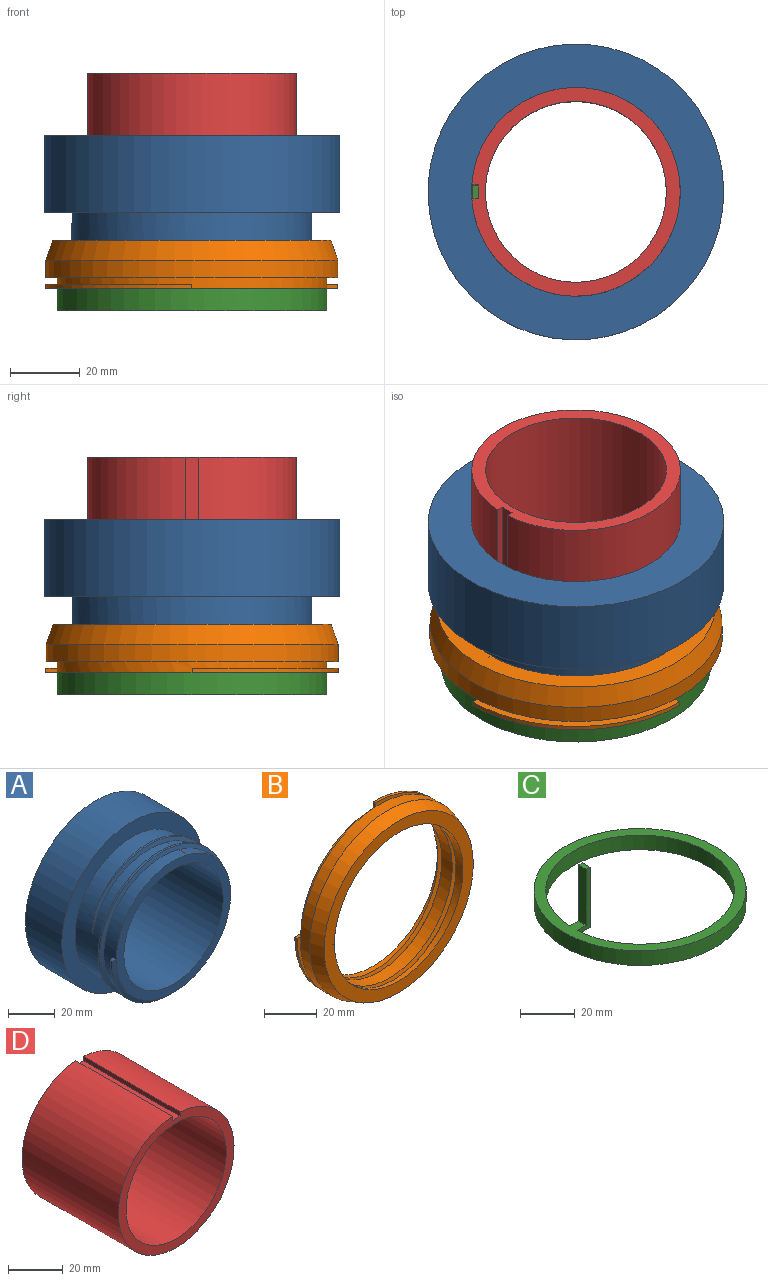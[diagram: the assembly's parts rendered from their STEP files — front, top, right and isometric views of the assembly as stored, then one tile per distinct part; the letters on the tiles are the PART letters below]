
ASSEMBLY  parts=4 mates=4
PART A: 13 faces, bbox 85.2x47.2x85.2 mm
  f0: bspline ~73x73mm, area 802.4mm2, adj f2,f4,f6,f8,f9
  f1: bspline ~73x73mm, area 892.7mm2, adj f2,f4,f5,f6,f8,f9
  f2: cylinder r=36.5mm len=73mm, axis (0,1,0), area 421.7mm2, adj f0,f1,f8,f9
  f3: cylinder r=30mm len=60mm, axis (0,1,0), area 8859.3mm2, adj f7,f11
  f4: cylinder r=34.5mm len=69mm, axis (0,1,0), area 2934.4mm2, adj f0,f1,f6,f9,f12
  f5: cylinder r=34.5mm len=69mm, axis (0,1,0), area 415.6mm2, adj f1,f6,f7
  f6: cylinder r=34.5mm len=69mm, axis (0,1,0), area 1270.9mm2, adj f0,f1,f4,f5,f7,f8
  f7: plane 69x69mm, normal (0,-1,0), area 911.8mm2, adj f3,f5,f6
  f8: plane 2x2mm, normal (0,0,1), area 3mm2, adj f0,f1,f2,f6
  f9: plane 42.8x30.41mm, normal (0,1,0), area 87.8mm2, adj f0,f1,f2,f4
  f10: cylinder r=42.5mm len=85mm, axis (0,-1,0), area 5874.8mm2, adj f11,f12
  f11: plane 85x85mm, normal (0,1,0), area 2847.1mm2, adj f3,f10
  f12: plane 85x85mm, normal (0,-1,0), area 1935.2mm2, adj f4,f10
PART B: 19 faces, bbox 84.1x14.9x84.1 mm
  f0: plane 84.13x84.13mm, normal (0,1,0), area 1296.7mm2, adj f1,f2,f7,f8,f9,f11,f12,f13
  f1: cylinder r=34.5mm len=69mm, axis (0,1,0), area 2253mm2, adj f0,f4,f15,f16,f18
  f2: cylinder r=38.75mm len=77.5mm, axis (0,1,0), area 584.3mm2, adj f0,f5,f7,f8,f10,f11,f12,f14
  f3: cylinder r=42mm len=84mm, axis (0,1,0), area 1319.5mm2, adj f5,f6
  f4: plane 80x80mm, normal (0,-1,0), area 1287.3mm2, adj f1,f6
  f5: plane 84x84mm, normal (0,1,0), area 824.5mm2, adj f2,f3
  f6: cone r=40mm half-angle=19.2deg, axis (0,1,0), area 1568.3mm2, adj f3,f4
  f7: plane 3.25x1.2mm, normal (-1,0,0), area 3.9mm2, adj f0,f2,f9,f10
  f8: plane 3.25x1.2mm, normal (0,0,-1), area 3.9mm2, adj f0,f2,f9,f10
  f9: cylinder r=42.07mm len=42mm, axis (0,1,0), area 79.1mm2, adj f0,f7,f8,f10
  f10: plane 42x42mm, normal (0,-1,0), area 204.6mm2, adj f2,f7,f8,f9
  f11: plane 3.25x1.2mm, normal (0,0,1), area 3.9mm2, adj f0,f2,f13,f14
  f12: plane 3.25x1.2mm, normal (1,0,0), area 3.9mm2, adj f0,f2,f13,f14
  f13: cylinder r=42.2mm len=42mm, axis (0,1,0), area 79.1mm2, adj f0,f11,f12,f14
  f14: plane 42x42mm, normal (0,-1,0), area 202.1mm2, adj f2,f11,f12,f13
  f15: bspline ~73x73mm, area 726.7mm2, adj f0,f1,f17,f18
  f16: bspline ~73x73mm, area 817.2mm2, adj f0,f1,f17,f18
  f17: cylinder r=36.5mm len=73mm, axis (0,1,0), area 384.8mm2, adj f0,f15,f16,f18
  f18: plane 2x2mm, normal (0,0,-1), area 3mm2, adj f1,f15,f16,f17
PART C: 10 faces, bbox 77.5x77.5x31.5 mm
  f0: plane 77.5x77.5mm, normal (0,0,1), area 996.6mm2, adj f1,f2,f5,f6,f8
  f1: cylinder r=34.5mm len=69mm, axis (0,0,-1), area 1401mm2, adj f0,f3,f4,f5,f6
  f2: cylinder r=38.75mm len=77.5mm, axis (0,0,-1), area 1582.6mm2, adj f0,f3
  f3: plane 77.5x77.5mm, normal (0,0,-1), area 978mm2, adj f1,f2
  f4: plane 6.67x4mm, normal (0,0,-1), area 26.6mm2, adj f1,f5,f6,f7
  f5: plane 27x6.61mm, normal (0,-1,0), area 63.2mm2, adj f0,f1,f4,f7,f8,f9
  f6: plane 27x6.61mm, normal (0,1,0), area 63.2mm2, adj f0,f1,f4,f7,f8,f9
  f7: plane 27x4mm, normal (1,0,0), area 108mm2, adj f4,f5,f6,f9
  f8: plane 25x4mm, normal (-1,0,0), area 100mm2, adj f0,f5,f6,f9
  f9: plane 4x2mm, normal (0,0,1), area 8mm2, adj f5,f6,f7,f8
PART D: 7 faces, bbox 60x50x59.9 mm
  f0: cylinder r=30mm len=60mm, axis (0,1,0), area 9224.6mm2, adj f1,f2,f4,f5
  f1: plane 60x59.93mm, normal (0,-1,0), area 695.8mm2, adj f0,f3,f4,f5,f6
  f2: plane 60x59.93mm, normal (0,1,0), area 695.8mm2, adj f0,f3,f4,f5,f6
  f3: cylinder r=26mm len=52mm, axis (0,1,0), area 8168.1mm2, adj f1,f2
  f4: plane 50x1.93mm, normal (-1,0,0), area 96.7mm2, adj f0,f1,f2,f6
  f5: plane 50x1.93mm, normal (1,0,0), area 96.7mm2, adj f0,f1,f2,f6
  f6: plane 50x4mm, normal (0,0,1), area 200mm2, adj f1,f2,f4,f5
PLACE A rot(axis=(0.46,-0.63,-0.63),130.7deg) t=(-24.87,-5.78,57.82)mm
PLACE B rot(axis=(-1,0,0),90deg) t=(-24.87,-5.78,36.05)mm fixed
PLACE C t=(-24.87,-5.78,29.55)mm
PLACE D rot(axis=(-0.58,-0.58,0.58),120deg) t=(-24.87,-5.78,47.85)mm
MATE parallel C.f5 <-> D.f5  axis (0,-1,0) through (-54.19,-7.78,45.73)mm
MATE fastened C.f1 <-> B.f1  axis (0,0,1) through (-24.87,-5.78,36.05)mm
MATE cylindrical A.f3 <-> B.f1  axis (0,0,1) through (-24.87,-5.78,79.82)mm
MATE cylindrical A.f3 <-> D.f3  axis (0,0,1) through (-24.87,-5.78,79.82)mm
